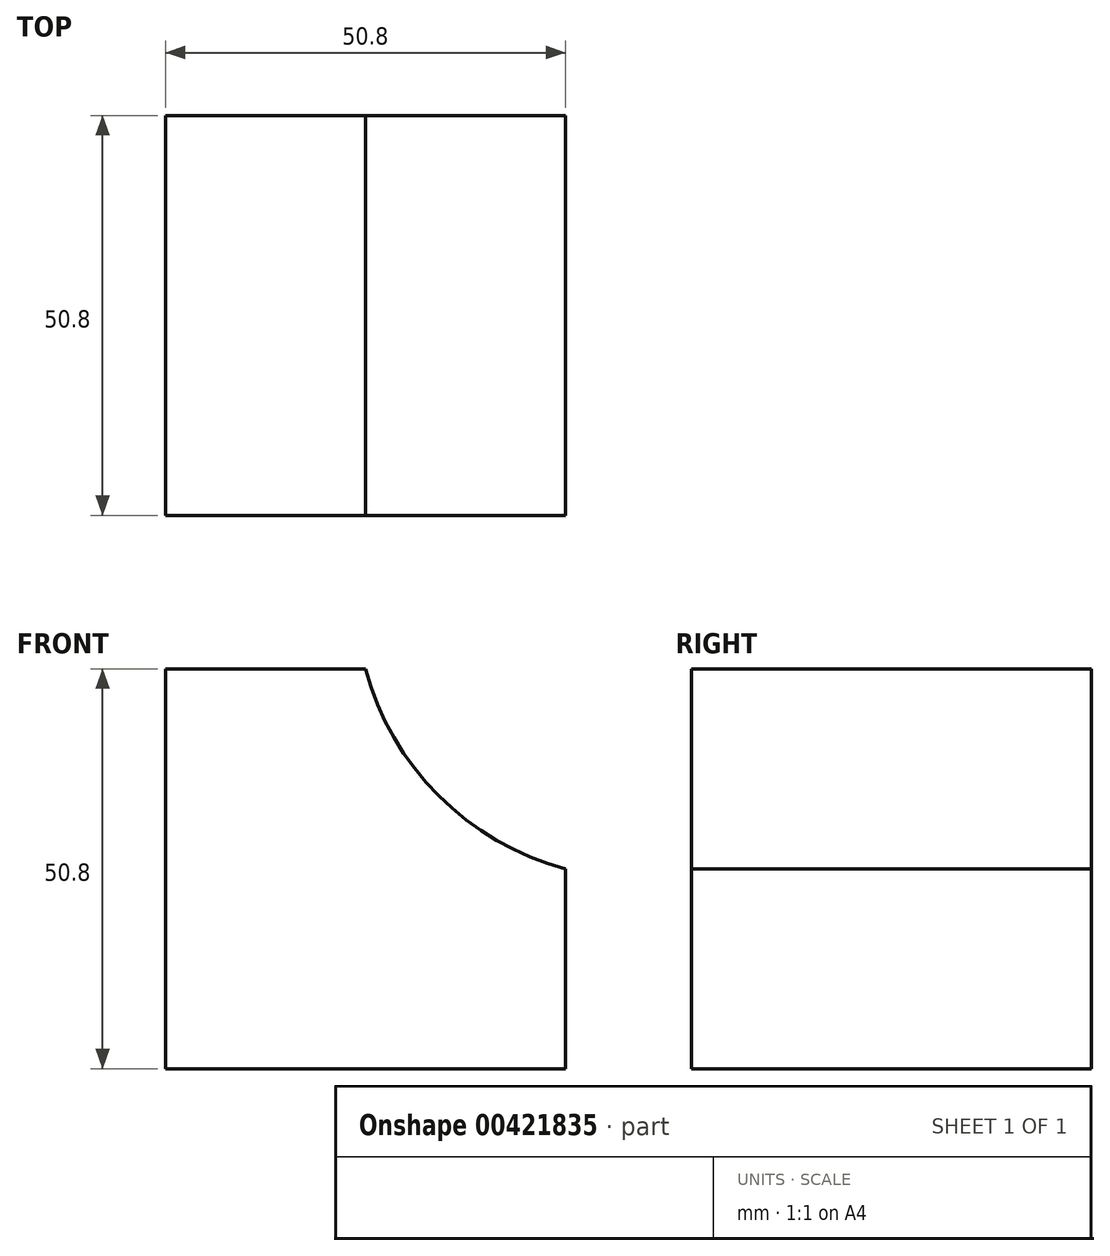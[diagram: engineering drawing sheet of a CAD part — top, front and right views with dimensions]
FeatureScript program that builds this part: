
annotation { "Feature Type Name" : "Feature", "Feature Type Description" : "" }
export const myFeature = defineFeature(function(context is Context, id is Id, definition is map)
    precondition{}
    {
        {
            var Q0;
            Q0=qCreatedBy(makeId("Front.planeOp"),FACE);
            var sketch = newSketch(context, id + "F0", { "sketchPlane" : qUnion([Q0])});
            skLineSegment(sketch, "E0", {"start": v(0, 0) * mm, "end": v(-50.8, 0) * mm});
            skLineSegment(sketch, "E1", {"start": v(-50.8, 0) * mm, "end": v(-50.8, 50.8) * mm});
            skLineSegment(sketch, "E2", {"start": v(-50.8, 50.8) * mm, "end": v(-25.4, 50.8) * mm});
            skLineSegment(sketch, "E3", {"start": v(0, 25.4) * mm, "end": v(0, 0) * mm});
            skArc(sketch, "E4", {"start": v(-25.4, 50.8) * mm, "mid": v(-16.12, 34.68) * mm, "end": v(0, 25.4) * mm});
            skSolve(sketch);
        }
        {
            var Q0;
            Q0 = qSketchRegion(id + "F0", true);
            extrude(context, id + "F1", {"entities" : qUnion([Q0]), "depth" : 50.8 * mm});
        }
    });
